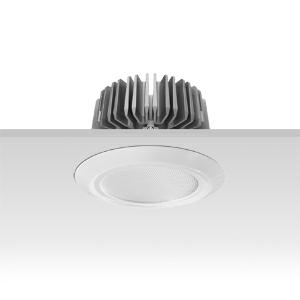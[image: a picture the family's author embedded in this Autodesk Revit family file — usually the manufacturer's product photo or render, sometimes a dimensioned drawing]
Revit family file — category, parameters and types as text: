
# Revit family: 3f_filippi_-_3f_reno_bianco_ampio_3f_filippi_-_30383_a01035_-_3f_reno_150_wh_3000-840_dali_wide___vs_wh_ae42
name_source: partatom
category: Lighting Fixtures
units: mm (PartAtom-declared; Revit-internal decimal feet)

## family parameters
Cut with Voids When Loaded = No
Host = Face
Light Source = No
Part Type = Normal
Room Calculation Point = No
Round Connector Dimension = Use Diameter
Shared = No

## types (1)
- 3F Filippi - 3F Reno Bianco Ampio (1 x LED, 2293 lm, 28 W, 4000 K)
    Apparent Load = 28 VA
    Approval mark = CE
    CIE Flux Codes = 74 93 99 100 100
    Color Rendering = 80
    Color Temperature = 4000 K
    Control Gear = Electronic transformer
    Default Elevation = 1800 mm
    Description = ILLUMINOTECHNICAL
Luminous efficiency 100% (DLOR 100%, ULOR 0%).
Initial luminous flux of the luminaire 2293 lm.
Direct symmetric wide distribution.
Installation Interdistance Transv.D = 1.12 x hu - Long.D = 1.11 x hu.
Tabular UGR (CIE 117 - 4H-8H; S=0.25H; 70/50/20): RUG 23.9 - 23.7.
Beam angle: 74° - 73°.
Luminous efficacy 82 lm/W.
Lifetime (L90/B10): 30000 h. (tq+25°C)
Lifetime (L85/B10): 50000 h. (tq+25°C)
Lifetime (L70/B10): 80000 h. (tq+25°C)
Sudden decreased luminous flux after 50000 hours: 0% (C0).
Photobiological safety in compliance with IEC/TR 62778: RG0 risk exempt, (IEC 62471).
In compliance with IEC/EN 62722-2-1 - IEC/EN 62717 standards.

SOURCE
Compact LED module 3000/840.
Energy efficiency class (UE 2019/2020 - UE 2019/2015): E.
CIE 13.3 Colour rendering index: CRI >80 (R9 <50%).
IES TM-30 Fidelity Index: Rf = 84 Rg = 95.
CCT nominal colour temperature 4000 K.
Colour initial tolerance (MacAdam): SDCM 3.
Zhaga Book 3 compliant.

MECHANICAL
Passive heat dissipator in die-casting aluminium, oversized, for optimum thermal management of the LED module.
Parabolic element with graduated/concentric rings in white polycarbonate.
Transparent external lens with glossy and satin differentiated surfaces, with a cooling and anti-insect system in methacrylate (PMMA).
Fastening spring clips in stainless steel.
Dimensions: diameter 176 mm, height 111 mm. Weight 1.44 kg.
IP44 protection degree for exposed part, IP20 for recessed part.
Mechanical strength to impacts IK06 (1 joule).
Glow-wire test resistance 650°C.

ELECTRICAL
Wiring on a separate unit.
Halogen Free DALI-2 DATI (Parts 251, 252, 253), PUSH-DIM, electronic wiring 230V-50/60Hz, power factor 0.97 at full load, THD <25%, constant output current, SELV, class II, 1 driver, 1 DALI addresse.
Power of the luminaire 28 W.
ENEC - CE.
SAFE FLICKER: PstLM=<1 and SVM=<0.4 (IEC TR 61547-1 and IEC TR 63158), to ensure a more comfortable and safe light.
Luminaire compliant with EN 60598-2-22 for power supply from a centralised emergency system CPSS (Central Power Supply System), not incorporated in the luminaire - high risk areas excluded. The default power and flux are 100% in AC and 100% in DC.
Ambient temperature from 0°C to +25°C.
Temperature class T6 max 85°C.
Relative humidity UR: <85%.

INSTALLATION
Pull-up recessed fitting.
False ceiling carving: 150 mm.
All accessories dedicated to this product are available on the Catalog and on our website www.3F-Filippi.com.

ACCESSORIES
A01035 - Anti-glare microprismatic VS moulded glass, tempered, not flammable, locked and in line with the trim, in white polycarbonate.

APPLICATIONS
Environments: architectural, commercial, exhibition areas, transit areas, corridors, shops, display windows, service areas.
In false ceilings with narrow voids.

LIGHT MANAGEMENT
Recommended minimum setting: 10%.
The luminaire, equipped with (DALI-2 DATI) driver, can be controlled manually with 3F Easy Dim technology or automatically/manually with wired or wireless DALI/D2D control systems.
The D2D driver guarantees interoperability with other devices with the same certification by making the following information available:
Device Data (Part 251), Energy Report (Part 252), Diagnosis & Maintenance (Part 253).
In electrical systems without a regulation system (manual or automatic) and DALI bus, a suitable jumper must be made on the DA-DA terminals of the appliance.

WARNING
Luminaire designed for disposal/recycling at end-of-life.
Replaceable (LED only) light source by a professional. Replaceable control gear by a professional.
    Height = 0 mm  [stored 0 ft]
    Lamp = 1 x LED
    Lamp Light Flux = 2293 lm
    Lamp Power = 28 W
    Lamp count = 1
    Length = 176 mm
    Lifetime = 50000 h
    Luminous efficacy = 82 lm/W
    Manufacturer = 3F Filippi
    ModVariant = No
    Model = 3F Filippi - 30383+A01035 - 3F Reno 150 WH 3000-840 DALI WIDE + VS WH
    Mounting Place = Ceiling
    Mounting Type = Recessed
    Number of Poles = 1
    OnlyDefault = Yes
    Power Factor = 1
    Product Name = 3F Filippi - 3F Reno Bianco Ampio
    Product group = recessed luminaire
    ProductGroupID = 4
    Protection Class = Protection class II
    Protection Degree = IP 20
    RLX_Detail_Level = 1
    RLX_Emergency_Light_Flux = 0 lm
    RLX_Emergency_Type = 0
    RLX_Emergency_Type_DB = No
    RlxData = <blob elided: 85237 chars, md5=527bbf22>
    Socket = socket
    Standby Power = 0 W
    System Light Flux = 2293 lm
    System Power = 28 W
    Type Comments = Product without accessories
    Type Image = 3ffilippi_3f_reno_150_wh_vs_smp.jpg
    URL = http://relux.com
    VarID = ---
    Voltage = 0 V
    Weight = 0.00 kg
    Width = 0 mm  [stored 0 ft]

note: [stored X ft] marks values corroborated as IEEE doubles in the binary element streams (Revit-internal decimal feet)

## geometry (parser evidence)
native form markers: Blend x4, Sweep x12
no freeform markers — native parametric forms only
